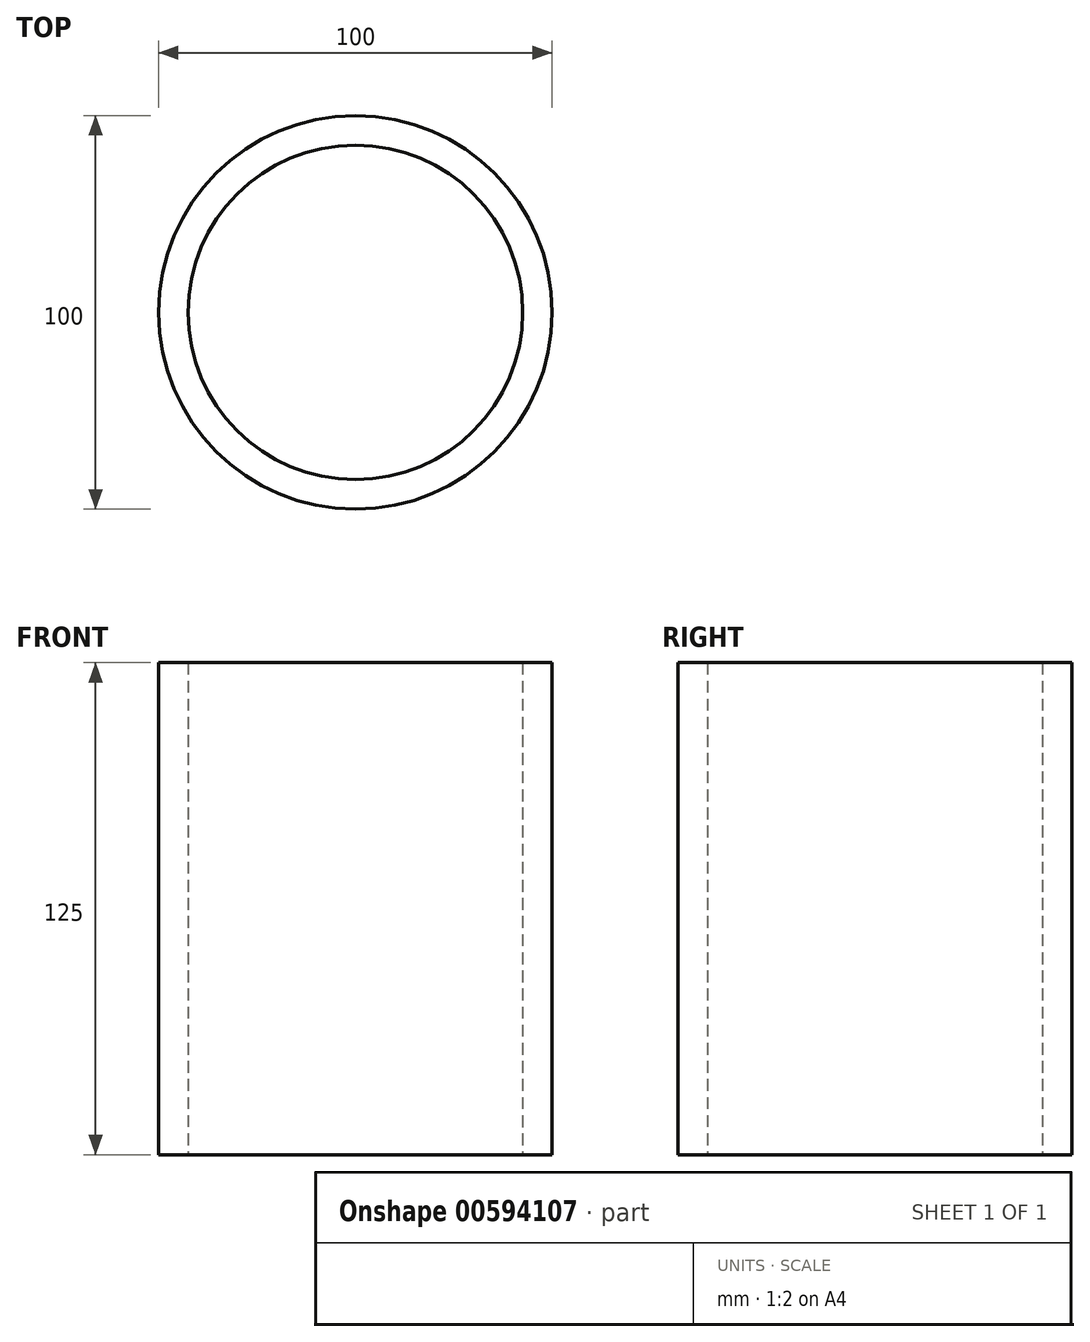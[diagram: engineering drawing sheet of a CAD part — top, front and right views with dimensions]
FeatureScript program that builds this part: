
annotation { "Feature Type Name" : "Feature", "Feature Type Description" : "" }
export const myFeature = defineFeature(function(context is Context, id is Id, definition is map)
    precondition{}
    {
        {
            var Q0;
            Q0=qCreatedBy(makeId("Top.planeOp"),FACE);
            var sketch = newSketch(context, id + "F0", { "sketchPlane" : qUnion([Q0])});
            skCircle(sketch, "E0", {"center": v(0, 0) * mm, "radius": 50 * mm});
            skCircle(sketch, "E1", {"center": v(0, 0) * mm, "radius": 42.5 * mm});
            skSolve(sketch);
        }
        {
            var Q0;
            Q0=makeQuery(id+"F0.imprint","IMPRINT",FACE,{"disambiguationData":[TD([[makeQuery(id+"F0.imprint","IMPRINT",EDGE,{"derivedFrom":sQuery(id+"F0.wireOp",EDGE,"E0")}),1.0]])]});
            extrude(context, id + "F1", {"entities" : qUnion([Q0]), "depth" : 125 * mm, "offsetDistance" : 25 * mm});
        }
        {
            var Q0;
            Q0=makeQuery(id+"F1.opExtrude","CAP_FACE",FACE,{"disambiguationData":[OSD([sQuery(id+"F0.wireOp",EDGE,"E0"),sQuery(id+"F0.wireOp",EDGE,"E1")])],"isStart":false});
            cPlane(context, id + "F2", {"entities" : qUnion([Q0]), "cplaneType" : CPlaneType.OFFSET, "offset" : 15 * mm, "width" : 150 * mm, "height" : 150 * mm});
        }
    });
